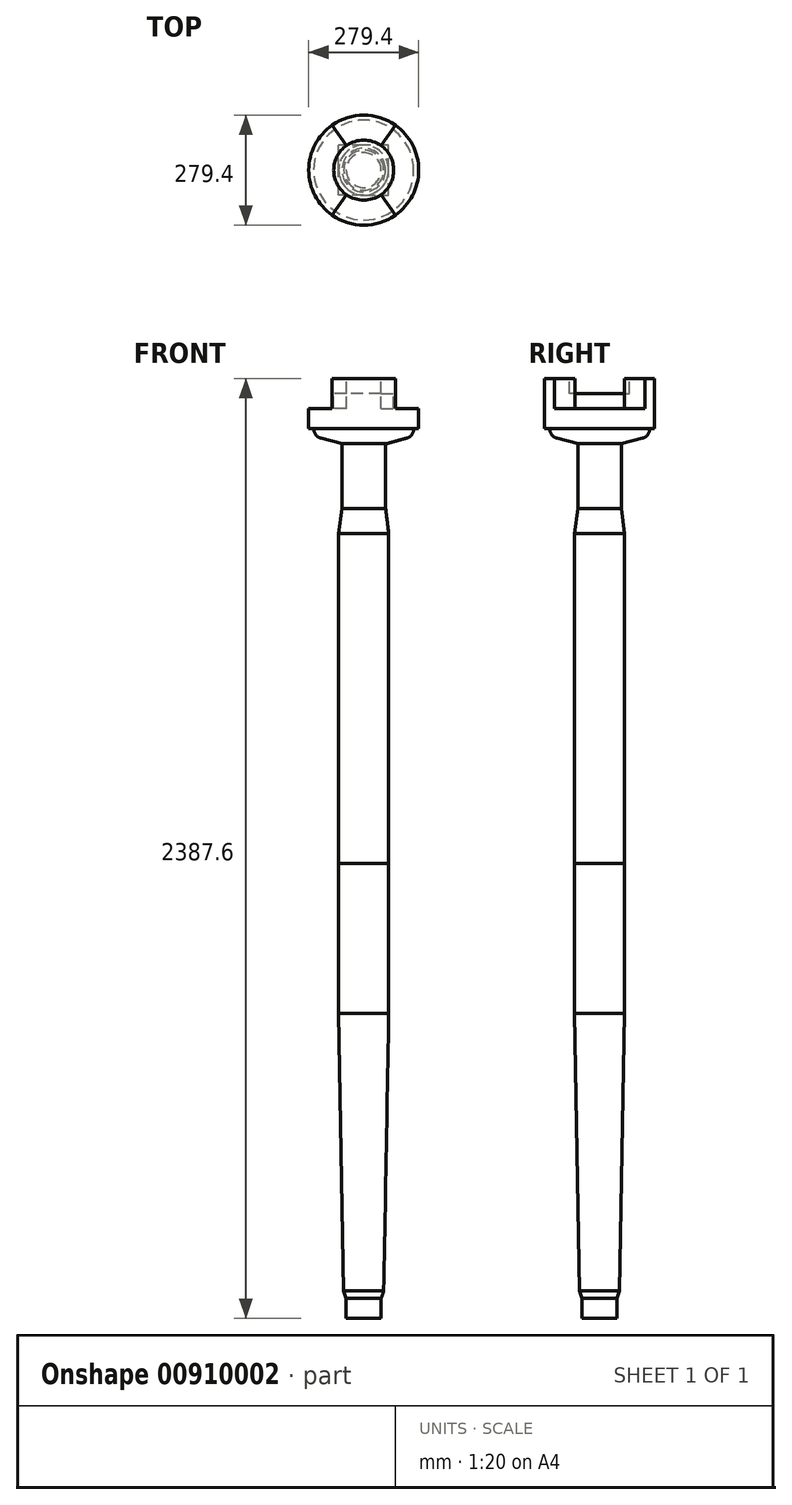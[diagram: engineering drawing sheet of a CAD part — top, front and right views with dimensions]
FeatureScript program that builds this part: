
annotation { "Feature Type Name" : "Feature", "Feature Type Description" : "" }
export const myFeature = defineFeature(function(context is Context, id is Id, definition is map)
    precondition{}
    {
        {
            var Q0;
            Q0=qCreatedBy(makeId("Front.planeOp"),FACE);
            var sketch = newSketch(context, id + "F0", { "sketchPlane" : qUnion([Q0])});
            skLineSegment(sketch, "E0", {"start": v(0, 0) * mm, "end": v(0, 774.7) * mm});
            skLineSegment(sketch, "E1", {"start": v(63.5, 774.7) * mm, "end": v(50.8, 69.85) * mm});
            skLineSegment(sketch, "E2", {"start": v(44.45, 0) * mm, "end": v(0, 0) * mm});
            skLineSegment(sketch, "E3", {"start": v(63.5, 774.7) * mm, "end": v(-63.5, 774.7) * mm});
            skLineSegment(sketch, "E4", {"start": v(-63.5, 774.7) * mm, "end": v(-63.5, 1155.7) * mm});
            skLineSegment(sketch, "E5", {"start": v(-63.5, 1155.7) * mm, "end": v(0, 1155.7) * mm});
            skLineSegment(sketch, "E6", {"start": v(63.5, 1155.7) * mm, "end": v(63.5, 774.7) * mm});
            skLineSegment(sketch, "E7", {"start": v(63.5, 1155.7) * mm, "end": v(63.5, 1993.9) * mm});
            skLineSegment(sketch, "E8", {"start": v(0, 2387.6) * mm, "end": v(0, 1155.7) * mm});
            skLineSegment(sketch, "E9", {"start": v(0, 1155.7) * mm, "end": v(63.5, 1155.7) * mm});
            skLineSegment(sketch, "E10", {"start": v(63.5, 1993.9) * mm, "end": v(55.56, 2057.4) * mm});
            skLineSegment(sketch, "E11", {"start": v(55.56, 2057.4) * mm, "end": v(55.56, 2221.97) * mm});
            skLineSegment(sketch, "E12", {"start": v(55.56, 2221.97) * mm, "end": v(108.17, 2236.07) * mm});
            skArc(sketch, "E13", {"start": v(108.17, 2236.07) * mm, "mid": v(121.75, 2245.14) * mm, "end": v(127, 2260.6) * mm});
            skLineSegment(sketch, "E14", {"start": v(127, 2260.6) * mm, "end": v(139.7, 2260.6) * mm});
            skLineSegment(sketch, "E15", {"start": v(139.7, 2260.6) * mm, "end": v(139.7, 2387.6) * mm});
            skLineSegment(sketch, "E16", {"start": v(139.7, 2387.6) * mm, "end": v(0, 2387.6) * mm});
            skLineSegment(sketch, "E17", {"start": v(44.45, 0) * mm, "end": v(44.45, 50.8) * mm});
            skLineSegment(sketch, "E18", {"start": v(44.45, 50.8) * mm, "end": v(50.8, 69.85) * mm});
            skSolve(sketch);
        }
        {
            var Q0;
            Q0=makeQuery(id+"F0.imprint","IMPRINT",FACE,{"disambiguationData":[TD([[makeQuery(id+"F0.imprint","IMPRINT",EDGE,{"derivedFrom":sQuery(id+"F0.wireOp",EDGE,"E7")}),1.0]])]});
            var Q1;
            {var subQ0=sQuery(id+"F0.wireOp",EDGE,"E0");Q1=makeQuery(id+"F0.imprint","IMPRINT",FACE,{"disambiguationData":[TD([[makeQuery(id+"F0.imprint","IMPRINT",EDGE,{"derivedFrom":subQ0}),-1.0]])]});}
            var Q2;
            Q2=sQuery(id+"F0.wireOp",EDGE,"E8");
            revolve(context, id + "F1", {"surfaceOperationType" : NewSurfaceOperationType.NEW, "entities" : qUnion([Q0, Q1]), "axis" : qUnion([Q2]), "revolveType" : RevolveType.FULL});
        }
        {
            var Q0;
            {var subQ0=sQuery(id+"F0.wireOp",EDGE,"E4");Q0=makeQuery(id+"F0.imprint","IMPRINT",FACE,{"disambiguationData":[TD([[makeQuery(id+"F0.imprint","IMPRINT",EDGE,{"derivedFrom":subQ0}),-1.0]])]});}
            extrude(context, id + "F2", {"entities" : qUnion([Q0]), "operationType" : NewBodyOperationType.ADD, "depth" : 127 * mm, "offsetDistance" : 25 * mm, "symmetric" : true});
        }
        {
            var Q0;
            Q0=makeQuery(id+"F1.opRevolve","SWEPT_FACE",FACE,{"disambiguationData":[OSD([sQuery(id+"F0.wireOp",EDGE,"E16")])]});
            var sketch = newSketch(context, id + "F3", { "sketchPlane" : qUnion([Q0])});
            skCircle(sketch, "E19", {"center": v(0, 0) * mm, "radius": 76.2 * mm});
            skLineSegment(sketch, "E20", {"start": v(-43.7, 62.42) * mm, "end": v(-80.13, 114.44) * mm});
            skLineSegment(sketch, "E21", {"start": v(43.7, 62.42) * mm, "end": v(80.13, 114.44) * mm});
            skCircle(sketch, "E22", {"center": v(0, 0) * mm, "radius": 139.7 * mm});
            skLineSegment(sketch, "E23", {"start": v(43.7, -62.42) * mm, "end": v(80.13, -114.44) * mm});
            skLineSegment(sketch, "E24", {"start": v(-43.7, -62.42) * mm, "end": v(-80.13, -114.44) * mm});
            skLineSegment(sketch, "E25", {"start": v(0, -2.84) * mm, "end": v(0, 139.7) * mm, "construction": true});
            skSolve(sketch);
        }
        {
            var Q0;
            {var subQ0=sQuery(id+"F3.wireOp",EDGE,"E19");var subQ1=makeQuery(id+"F3.imprint","INTERSECT",VERTEX,{"derivedFrom":[subQ0,sQuery(id+"F3.wireOp",EDGE,"E20")]});Q0=makeQuery(id+"F3.imprint","IMPRINT",FACE,{"disambiguationData":[TD([[makeQuery(id+"F3.imprint","IMPRINT",EDGE,{"disambiguationData":[TD([[subQ1,1.0]])],"derivedFrom":subQ0}),1.0]])]});}
            extrude(context, id + "F4", {"entities" : qUnion([Q0]), "operationType" : NewBodyOperationType.REMOVE, "oppositeDirection" : true, "depth" : 38.1 * mm, "offsetDistance" : 25 * mm});
        }
        {
            var Q0;
            {var subQ0=sQuery(id+"F3.wireOp",EDGE,"E20");Q0=makeQuery(id+"F3.imprint","IMPRINT",FACE,{"disambiguationData":[TD([[makeQuery(id+"F3.imprint","IMPRINT",EDGE,{"derivedFrom":subQ0}),1.0]])]});}
            var Q1;
            {var subQ0=sQuery(id+"F3.wireOp",EDGE,"E21");Q1=makeQuery(id+"F3.imprint","IMPRINT",FACE,{"disambiguationData":[TD([[makeQuery(id+"F3.imprint","IMPRINT",EDGE,{"derivedFrom":subQ0}),-1.0]])]});}
            extrude(context, id + "F5", {"entities" : qUnion([Q0, Q1]), "operationType" : NewBodyOperationType.REMOVE, "oppositeDirection" : true, "depth" : 76.2 * mm, "offsetDistance" : 25 * mm});
        }
    });
